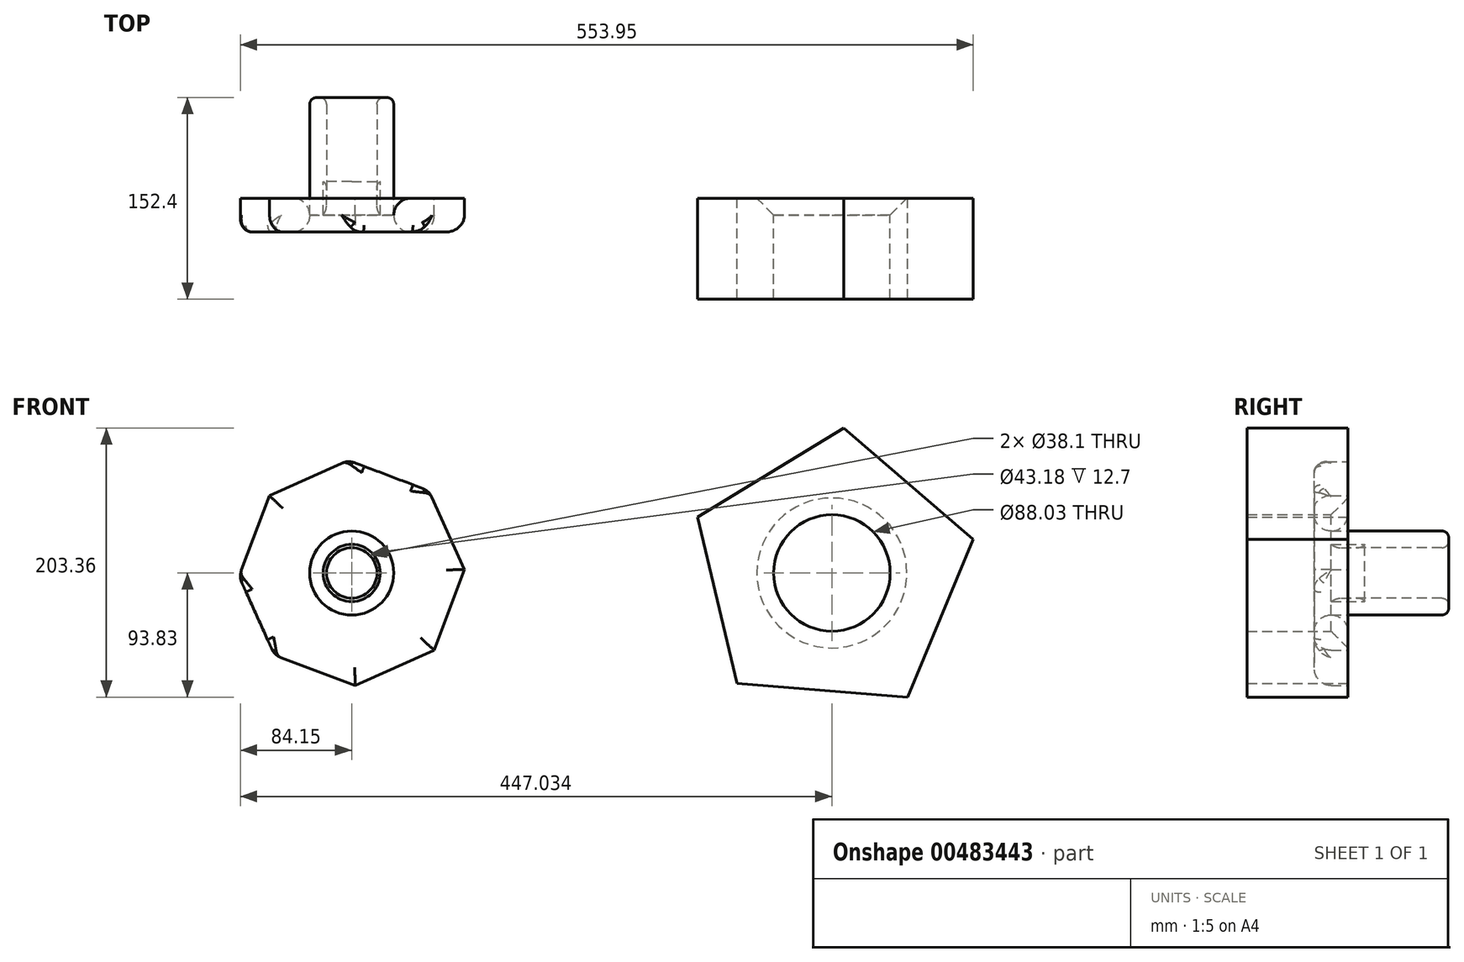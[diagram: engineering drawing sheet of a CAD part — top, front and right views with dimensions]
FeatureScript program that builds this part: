
annotation { "Feature Type Name" : "Feature", "Feature Type Description" : "" }
export const myFeature = defineFeature(function(context is Context, id is Id, definition is map)
    precondition{}
    {
        {
            var Q0;
            Q0=qCreatedBy(makeId("Front.planeOp"),FACE);
            var sketch = newSketch(context, id + "F0", { "sketchPlane" : qUnion([Q0])});
            skCircle(sketch, "E0", {"center": v(0, 0) * mm, "radius": 31.75 * mm});
            skCircle(sketch, "E1", {"center": v(0, 0) * mm, "radius": 19.05 * mm});
            skSolve(sketch);
        }
        {
            var Q0;
            Q0=makeQuery(id+"F0.imprint","IMPRINT",FACE,{"disambiguationData":[TD([[makeQuery(id+"F0.imprint","IMPRINT",EDGE,{"derivedFrom":sQuery(id+"F0.wireOp",EDGE,"E1")}),1.0]])]});
            var Q1;
            Q1=makeQuery(id+"F0.imprint","IMPRINT",FACE,{"disambiguationData":[TD([[makeQuery(id+"F0.imprint","IMPRINT",EDGE,{"derivedFrom":sQuery(id+"F0.wireOp",EDGE,"E0")}),1.0]])]});
            var Q2;
            Q2=sQuery(id+"F0.wireOp",EDGE,"E0");
            extrude(context, id + "F1", {"entities" : qUnion([Q0, Q1]), "bodyType" : ToolBodyType.SURFACE, "operationType" : NewBodyOperationType.INTERSECT, "surfaceEntities" : qUnion([Q2]), "oppositeDirection" : true, "depth" : 76.2 * mm});
        }
        {
            var Q0;
            Q0=qCreatedBy(makeId("Front.planeOp"),FACE);
            var sketch = newSketch(context, id + "F2", { "sketchPlane" : qUnion([Q0])});
            skCircle(sketch, "E2", {"center": v(362.88, 0) * mm, "radius": 44.02 * mm});
            skCircle(sketch, "E3", {"center": v(362.88, 0) * mm, "radius": 88.9 * mm});
            skCircle(sketch, "E4.cCircle", {"center": v(362.88, 0) * mm, "radius": 88.9 * mm, "construction": true});
            skLineSegment(sketch, "E4.0", {"start": v(469.8, 25.4) * mm, "end": v(420.07, -93.83) * mm});
            skLineSegment(sketch, "E4.1", {"start": v(420.07, -93.83) * mm, "end": v(291.32, -83.39) * mm});
            skLineSegment(sketch, "E4.2", {"start": v(291.32, -83.39) * mm, "end": v(261.46, 42.3) * mm});
            skLineSegment(sketch, "E4.3", {"start": v(261.46, 42.3) * mm, "end": v(371.77, 109.53) * mm});
            skLineSegment(sketch, "E4.4", {"start": v(371.77, 109.53) * mm, "end": v(469.8, 25.4) * mm});
            skPoint(sketch, "E4.0.midPoint", {"position": v(444.93, -34.22) * mm});
            skSolve(sketch);
        }
        {
            var Q0;
            {var subQ0=sQuery(id+"F2.wireOp",EDGE,"E4.4");var subQ1=sQuery(id+"F2.wireOp",EDGE,"E3");var subQ2=makeQuery(id+"F2.imprint","INTERSECT",VERTEX,{"derivedFrom":[subQ1,subQ0]});Q0=makeQuery(id+"F2.imprint","IMPRINT",FACE,{"disambiguationData":[TD([[makeQuery(id+"F2.imprint","IMPRINT",EDGE,{"disambiguationData":[TD([[subQ2,1.0]])],"derivedFrom":subQ1}),-1.0]])]});}
            var Q1;
            Q1=makeQuery(id+"F2.imprint","IMPRINT",FACE,{"disambiguationData":[TD([[makeQuery(id+"F2.imprint","IMPRINT",EDGE,{"derivedFrom":sQuery(id+"F2.wireOp",EDGE,"E2")}),-1.0]])]});
            var Q2;
            {var subQ0=sQuery(id+"F2.wireOp",EDGE,"E4.3");var subQ1=sQuery(id+"F2.wireOp",EDGE,"E3");var subQ2=makeQuery(id+"F2.imprint","INTERSECT",VERTEX,{"derivedFrom":[subQ1,subQ0]});Q2=makeQuery(id+"F2.imprint","IMPRINT",FACE,{"disambiguationData":[TD([[makeQuery(id+"F2.imprint","IMPRINT",EDGE,{"disambiguationData":[TD([[subQ2,1.0]])],"derivedFrom":subQ1}),-1.0]])]});}
            var Q3;
            {var subQ0=sQuery(id+"F2.wireOp",EDGE,"E4.1");var subQ1=sQuery(id+"F2.wireOp",EDGE,"E3");var subQ2=makeQuery(id+"F2.imprint","INTERSECT",VERTEX,{"derivedFrom":[subQ1,subQ0]});Q3=makeQuery(id+"F2.imprint","IMPRINT",FACE,{"disambiguationData":[TD([[makeQuery(id+"F2.imprint","IMPRINT",EDGE,{"disambiguationData":[TD([[subQ2,-1.0]])],"derivedFrom":subQ1}),-1.0]])]});}
            var Q4;
            {var subQ0=sQuery(id+"F2.wireOp",EDGE,"E4.2");var subQ1=sQuery(id+"F2.wireOp",EDGE,"E3");var subQ2=makeQuery(id+"F2.imprint","INTERSECT",VERTEX,{"derivedFrom":[subQ1,subQ0]});Q4=makeQuery(id+"F2.imprint","IMPRINT",FACE,{"disambiguationData":[TD([[makeQuery(id+"F2.imprint","IMPRINT",EDGE,{"disambiguationData":[TD([[subQ2,-1.0]])],"derivedFrom":subQ1}),-1.0]])]});}
            var Q5;
            {var subQ0=sQuery(id+"F2.wireOp",EDGE,"E4.3");var subQ1=sQuery(id+"F2.wireOp",EDGE,"E3");var subQ2=makeQuery(id+"F2.imprint","INTERSECT",VERTEX,{"derivedFrom":[subQ1,subQ0]});Q5=makeQuery(id+"F2.imprint","IMPRINT",FACE,{"disambiguationData":[TD([[makeQuery(id+"F2.imprint","IMPRINT",EDGE,{"disambiguationData":[TD([[subQ2,-1.0]])],"derivedFrom":subQ1}),-1.0]])]});}
            extrude(context, id + "F3", {"entities" : qUnion([Q0, Q1, Q2, Q3, Q4, Q5]), "depth" : 76.2 * mm});
        }
        {
            var Q0;
            Q0=makeQuery(id+"F3.opExtrude","CAP_EDGE",EDGE,{"disambiguationData":[OSD([sQuery(id+"F2.wireOp",EDGE,"E2")])],"isStart":true});
            chamfer(context, id + "F4", {"entities" : qUnion([Q0]), "width" : 12.7 * mm, "tangentPropagation" : true});
        }
        {
            var Q0;
            Q0=qCreatedBy(makeId("Front.planeOp"),FACE);
            var sketch = newSketch(context, id + "F5", { "sketchPlane" : qUnion([Q0])});
            skCircle(sketch, "E5.cCircle", {"center": v(0, 0) * mm, "radius": 78.74 * mm, "construction": true});
            skLineSegment(sketch, "E5.0", {"start": v(-2.68, 85.19) * mm, "end": v(58.34, 62.13) * mm});
            skLineSegment(sketch, "E5.1", {"start": v(58.34, 62.13) * mm, "end": v(85.19, 2.68) * mm});
            skLineSegment(sketch, "E5.2", {"start": v(85.19, 2.68) * mm, "end": v(62.13, -58.34) * mm});
            skLineSegment(sketch, "E5.3", {"start": v(62.13, -58.34) * mm, "end": v(2.68, -85.19) * mm});
            skLineSegment(sketch, "E5.4", {"start": v(2.68, -85.19) * mm, "end": v(-58.34, -62.13) * mm});
            skLineSegment(sketch, "E5.5", {"start": v(-58.34, -62.13) * mm, "end": v(-85.19, -2.68) * mm});
            skLineSegment(sketch, "E5.6", {"start": v(-85.19, -2.68) * mm, "end": v(-62.13, 58.34) * mm});
            skLineSegment(sketch, "E5.7", {"start": v(-62.13, 58.34) * mm, "end": v(-2.68, 85.19) * mm});
            skPoint(sketch, "E5.0.midPoint", {"position": v(27.83, 73.66) * mm});
            skCircle(sketch, "E6", {"center": v(0, 0) * mm, "radius": 50.8 * mm});
            skSolve(sketch);
        }
        {
            var Q0;
            Q0=makeQuery(id+"F5.imprint","IMPRINT",FACE,{"disambiguationData":[TD([[makeQuery(id+"F5.imprint","IMPRINT",EDGE,{"derivedFrom":sQuery(id+"F5.wireOp",EDGE,"E5.0")}),-1.0]])]});
            extrude(context, id + "F6", {"entities" : qUnion([Q0]), "depth" : 25.4 * mm});
        }
        {
            var Q0;
            Q0=qCreatedBy(makeId("Front.planeOp"),FACE);
            var sketch = newSketch(context, id + "F7", { "sketchPlane" : qUnion([Q0])});
            skCircle(sketch, "E7", {"center": v(0, 0) * mm, "radius": 31.75 * mm});
            skCircle(sketch, "E8", {"center": v(0, 0) * mm, "radius": 57.15 * mm});
            skSolve(sketch);
        }
        {
            var Q0;
            Q0=qCreatedBy(makeId("Front.planeOp"),FACE);
            var sketch = newSketch(context, id + "F8", { "sketchPlane" : qUnion([Q0])});
            skCircle(sketch, "E9", {"center": v(0, 0) * mm, "radius": 19.05 * mm});
            skCircle(sketch, "E10", {"center": v(0, 0) * mm, "radius": 21.59 * mm});
            skSolve(sketch);
        }
        {
            var Q0;
            Q0 = qSketchRegion(id + "F8", true);
            extrude(context, id + "F9", {"entities" : qUnion([Q0]), "endBound" : BoundingType.SYMMETRIC, "depth" : 25.4 * mm});
        }
        {
            var Q0;
            Q0 = qSketchRegion(id + "F5", true);
            extrude(context, id + "F10", {"entities" : qUnion([Q0]), "operationType" : NewBodyOperationType.ADD, "depth" : 25.4 * mm});
        }
        {
            var Q0;
            Q0=makeQuery(id+"F6.opExtrude","CAP_EDGE",EDGE,{"disambiguationData":[OSD([sQuery(id+"F5.wireOp",EDGE,"E5.0")])],"isStart":false});
            var Q1;
            Q1=makeQuery(id+"F6.opExtrude","CAP_EDGE",EDGE,{"disambiguationData":[OSD([sQuery(id+"F5.wireOp",EDGE,"E6")])],"isStart":false});
            var Q2;
            Q2=makeQuery(id+"F6.opExtrude","CAP_EDGE",EDGE,{"disambiguationData":[OSD([sQuery(id+"F5.wireOp",EDGE,"E5.5")])],"isStart":false});
            var Q3;
            Q3=makeQuery(id+"F1.opExtrude","SWEPT_FACE",FACE,{"disambiguationData":[OSD([sQuery(id+"F0.wireOp",EDGE,"E0")])]});
            fillet(context, id + "F11", {"entities" : qUnion([Q0, Q1, Q2, Q3]), "radius" : 5.08 * mm, "rho" : 0.5, "crossSection" : FilletCrossSection.CONIC, "allowEdgeOverflow" : false});
        }
        {
            var Q0;
            Q0 = qSketchRegion(id + "F7", true);
            extrude(context, id + "F12", {"entities" : qUnion([Q0]), "operationType" : NewBodyOperationType.ADD, "depth" : 25.4 * mm});
        }
        {
            var Q0;
            Q0=makeQuery(id+"F12.opExtrude","SWEPT_FACE",FACE,{"disambiguationData":[OSD([sQuery(id+"F7.wireOp",EDGE,"E7")])]});
            var Q1;
            Q1=makeQuery(id+"F12.opExtrude","CAP_EDGE",EDGE,{"disambiguationData":[OSD([sQuery(id+"F7.wireOp",EDGE,"E7")])],"isStart":false});
            var Q2;
            Q2=makeQuery(id+"F12.boolean.opBoolean","MERGE",FACE,{"derivedFrom":[makeQuery(id+"F6.opExtrude","CAP_FACE",FACE,{"disambiguationData":[OSD([sQuery(id+"F5.wireOp",EDGE,"E5.0"),sQuery(id+"F5.wireOp",EDGE,"E5.1"),sQuery(id+"F5.wireOp",EDGE,"E5.2"),sQuery(id+"F5.wireOp",EDGE,"E5.3"),sQuery(id+"F5.wireOp",EDGE,"E5.4"),sQuery(id+"F5.wireOp",EDGE,"E5.5"),sQuery(id+"F5.wireOp",EDGE,"E5.6"),sQuery(id+"F5.wireOp",EDGE,"E5.7"),sQuery(id+"F5.wireOp",EDGE,"E6")])],"isStart":false}),makeQuery(id+"F12.opExtrude","CAP_FACE",FACE,{"disambiguationData":[OSD([sQuery(id+"F7.wireOp",EDGE,"E7"),sQuery(id+"F7.wireOp",EDGE,"E8")])],"isStart":false})]});
            fillet(context, id + "F13", {"entities" : qUnion([Q0, Q1, Q2]), "radius" : 12.7 * mm, "tangentPropagation" : true, "allowEdgeOverflow" : false});
        }
        {
            var Q0;
            Q0=makeQuery(id+"F1.opExtrude","SWEPT_FACE",FACE,{"disambiguationData":[OSD([sQuery(id+"F0.wireOp",EDGE,"E0")])]});
            var Q1;
            Q1=makeQuery(id+"F9.opExtrude","CAP_EDGE",EDGE,{"disambiguationData":[OSD([sQuery(id+"F8.wireOp",EDGE,"E9")])],"isStart":false});
            fillet(context, id + "F14", {"entities" : qUnion([Q0, Q1]), "radius" : 12.7 * mm, "tangentPropagation" : true, "allowEdgeOverflow" : false});
        }
        {
            var Q0;
            Q0=qCreatedBy(makeId("Front.planeOp"),FACE);
            var sketch = newSketch(context, id + "F15", { "sketchPlane" : qUnion([Q0])});
            skCircle(sketch, "E11", {"center": v(0, 0) * mm, "radius": 21.59 * mm});
            skCircle(sketch, "E12", {"center": v(0, 0) * mm, "radius": 31.75 * mm});
            skSolve(sketch);
        }
        {
            var Q0;
            Q0 = qSketchRegion(id + "F15", true);
            extrude(context, id + "F16", {"entities" : qUnion([Q0]), "depth" : 12.7 * mm});
        }
        {
            var Q0;
            Q0 = qSketchRegion(id + "F0", true);
            extrude(context, id + "F17", {"entities" : qUnion([Q0]), "oppositeDirection" : true, "depth" : 76.2 * mm});
        }
        {
            var Q0;
            Q0=makeQuery(id+"F17.opExtrude","CAP_FACE",FACE,{"disambiguationData":[OSD([sQuery(id+"F0.wireOp",EDGE,"E0"),sQuery(id+"F0.wireOp",EDGE,"E1")])],"isStart":false});
            var Q1;
            Q1=makeQuery(id+"F1.opExtrude","SWEPT_FACE",FACE,{"disambiguationData":[OSD([sQuery(id+"F0.wireOp",EDGE,"E0")])]});
            fillet(context, id + "F18", {"entities" : qUnion([Q0, Q1]), "radius" : 5.08 * mm, "tangentPropagation" : true, "allowEdgeOverflow" : false});
        }
        {
            var Q0;
            Q0=makeQuery(id+"F9.opExtrude","CAP_EDGE",EDGE,{"disambiguationData":[OSD([sQuery(id+"F8.wireOp",EDGE,"E9")])],"isStart":true});
            var Q1;
            {var subQ0=sQuery(id+"F8.wireOp",EDGE,"E9");Q1=makeQuery(id+"F14.opFillet","BLEND_EDGE",EDGE,{"blendedFrom":[makeQuery(id+"F9.opExtrude","CAP_EDGE",EDGE,{"disambiguationData":[OSD([subQ0])],"isStart":false}),makeQuery(id+"F9.opExtrude","SWEPT_FACE",FACE,{"disambiguationData":[OSD([subQ0])]})],"blendedInto":[makeQuery(id+"F9.opExtrude","SWEPT_FACE",FACE,{"disambiguationData":[OSD([subQ0])]})]});}
            fillet(context, id + "F19", {"entities" : qUnion([Q0, Q1]), "radius" : 5.08 * mm, "tangentPropagation" : true, "allowEdgeOverflow" : false});
        }
    });
